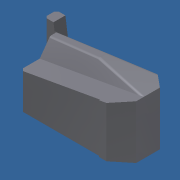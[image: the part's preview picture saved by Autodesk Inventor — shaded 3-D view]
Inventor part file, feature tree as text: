
AUTODESK INVENTOR PART (.ipt)
format: ipt  version: unknown  size: 313,344 bytes
history: native  units: mm
features: sketch x8, extrude x6, chamfer x3, fillet x2, other x2, sweep x1, projected_geometry x1
ambient origin geometry x8: Origin, YZ Plane, XZ Plane, XY Plane, X Axis, Y Axis, Z Axis, Center Point
feature tree (23):
  extrude  "Выдавливание1"  Depth=17.0mm
  extrude  "Выдавливание2"  Depth=16.3mm
  extrude  "Выдавливание3"  Depth=39.0mm
  sweep  "Сдвиг1"
  extrude  "Выдавливание4"  Depth=4.0mm
  fillet  "Сопряжение1"  Radius=8.0mm
  fillet  "Сопряжение2"  Radius=5.5mm
  other  "РабПлоскость1"
  extrude  "Выдавливание5"  Depth=5.5mm
  extrude  "Выдавливание6"  Depth=8.0mm
  chamfer  "Фаска1"  Distance=0.75mm
  chamfer  "Фаска2"  Distance=0.75mm
  chamfer  "Фаска3"  Distance=0.75mm
  sketch  "Эскиз1"
  sketch  "Эскиз2"
  sketch  "Эскиз3"
  sketch  "Эскиз4"
  sketch  "Эскиз5"
  sketch  "Эскиз6"
  sketch  "Эскиз8"
  projected_geometry  "Спроецированная петля5"
  sketch  "Эскиз9"
  other  "Проецирование ребер1"
